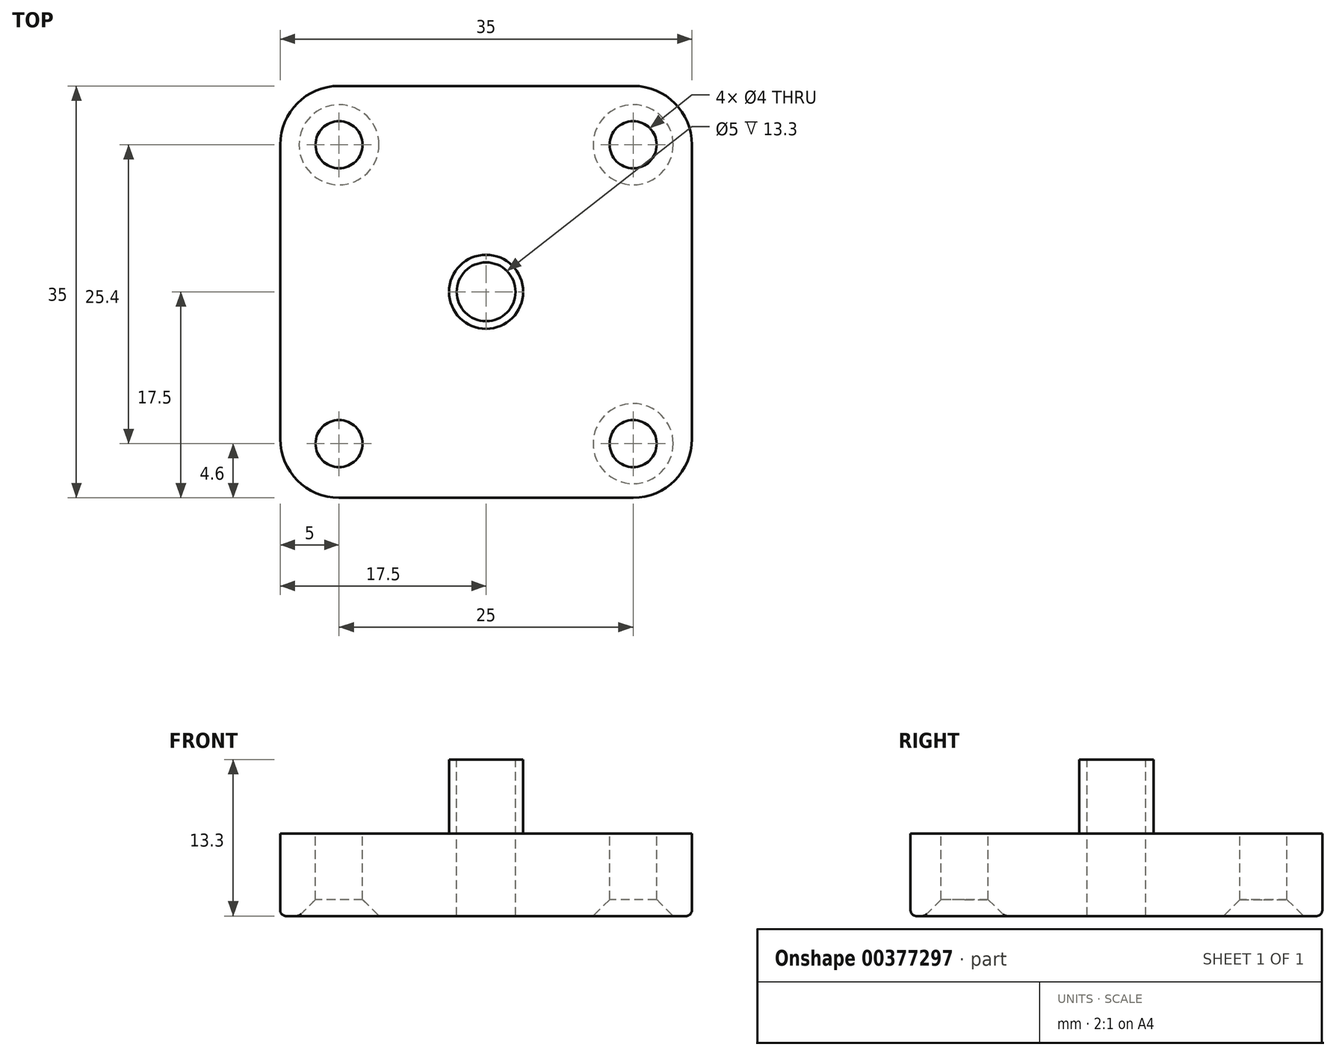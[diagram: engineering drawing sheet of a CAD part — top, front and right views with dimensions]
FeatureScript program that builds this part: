
annotation { "Feature Type Name" : "Feature", "Feature Type Description" : "" }
export const myFeature = defineFeature(function(context is Context, id is Id, definition is map)
    precondition{}
    {
        {
            var Q0;
            Q0=qCreatedBy(makeId("Top.planeOp"),FACE);
            var sketch = newSketch(context, id + "F0", { "sketchPlane" : qUnion([Q0])});
            skLineSegment(sketch, "E0.bottom", {"start": v(17.5, 17.5) * mm, "end": v(-17.5, 17.5) * mm});
            skLineSegment(sketch, "E0.top", {"start": v(17.5, -17.5) * mm, "end": v(-17.5, -17.5) * mm});
            skLineSegment(sketch, "E0.left", {"start": v(17.5, 17.5) * mm, "end": v(17.5, -17.5) * mm});
            skLineSegment(sketch, "E0.right", {"start": v(-17.5, 17.5) * mm, "end": v(-17.5, -17.5) * mm});
            skPoint(sketch, "E0.middle", {"position": v(0, 0) * mm});
            skSolve(sketch);
        }
        {
            var Q0;
            Q0=makeQuery(id+"F0.imprint","IMPRINT",FACE,{"disambiguationData":[TD([[makeQuery(id+"F0.imprint","IMPRINT",EDGE,{"derivedFrom":sQuery(id+"F0.wireOp",EDGE,"E0.bottom")}),1.0]])]});
            extrude(context, id + "F1", {"entities" : qUnion([Q0]), "endBound" : BoundingType.SYMMETRIC, "depth" : 7 * mm});
        }
        {
            var Q0;
            Q0=makeQuery(id+"F1.opExtrude","CAP_FACE",FACE,{"disambiguationData":[OSD([sQuery(id+"F0.wireOp",EDGE,"E0.bottom"),sQuery(id+"F0.wireOp",EDGE,"E0.top"),sQuery(id+"F0.wireOp",EDGE,"E0.left"),sQuery(id+"F0.wireOp",EDGE,"E0.right")])],"isStart":false});
            var sketch = newSketch(context, id + "F2", { "sketchPlane" : qUnion([Q0])});
            skCircle(sketch, "E1", {"center": v(-12.5, -12.9) * mm, "radius": 2 * mm});
            skCircle(sketch, "E2", {"center": v(-12.5, 12.5) * mm, "radius": 2 * mm});
            skCircle(sketch, "E3", {"center": v(12.5, 12.5) * mm, "radius": 2 * mm});
            skCircle(sketch, "E4", {"center": v(12.5, -12.9) * mm, "radius": 2 * mm});
            skSolve(sketch);
        }
        {
            var Q0;
            Q0 = qSketchRegion(id + "F2", true);
            extrude(context, id + "F3", {"entities" : qUnion([Q0]), "operationType" : NewBodyOperationType.REMOVE, "endBound" : BoundingType.THROUGH_ALL, "oppositeDirection" : true, "depth" : 25 * mm});
        }
        {
            var Q0;
            Q0=makeQuery(id+"F1.opExtrude","SWEPT_EDGE",EDGE,{"disambiguationData":[OSD([sQuery(id+"F0.wireOp",EDGE,"E0.bottom"),sQuery(id+"F0.wireOp",EDGE,"E0.right")])]});
            var Q1;
            Q1=makeQuery(id+"F1.opExtrude","SWEPT_EDGE",EDGE,{"disambiguationData":[OSD([sQuery(id+"F0.wireOp",EDGE,"E0.bottom"),sQuery(id+"F0.wireOp",EDGE,"E0.left")])]});
            var Q2;
            Q2=makeQuery(id+"F1.opExtrude","SWEPT_EDGE",EDGE,{"disambiguationData":[OSD([sQuery(id+"F0.wireOp",EDGE,"E0.top"),sQuery(id+"F0.wireOp",EDGE,"E0.left")])]});
            var Q3;
            Q3=makeQuery(id+"F1.opExtrude","SWEPT_EDGE",EDGE,{"disambiguationData":[OSD([sQuery(id+"F0.wireOp",EDGE,"E0.top"),sQuery(id+"F0.wireOp",EDGE,"E0.right")])]});
            fillet(context, id + "F4", {"entities" : qUnion([Q0, Q1, Q2, Q3]), "radius" : 5 * mm, "tangentPropagation" : true, "allowEdgeOverflow" : false});
        }
        {
            var Q0;
            Q0=makeQuery(id+"F1.opExtrude","CAP_FACE",FACE,{"disambiguationData":[OSD([sQuery(id+"F0.wireOp",EDGE,"E0.bottom"),sQuery(id+"F0.wireOp",EDGE,"E0.top"),sQuery(id+"F0.wireOp",EDGE,"E0.left"),sQuery(id+"F0.wireOp",EDGE,"E0.right")])],"isStart":false});
            var sketch = newSketch(context, id + "F5", { "sketchPlane" : qUnion([Q0])});
            skCircle(sketch, "E5", {"center": v(0, 0) * mm, "radius": 3.15 * mm});
            skSolve(sketch);
        }
        {
            var Q0;
            Q0 = qSketchRegion(id + "F5", true);
            extrude(context, id + "F6", {"entities" : qUnion([Q0]), "operationType" : NewBodyOperationType.ADD, "depth" : 6.3 * mm});
        }
        {
            var Q0;
            Q0=makeQuery(id+"F6.opExtrude","CAP_FACE",FACE,{"disambiguationData":[OSD([sQuery(id+"F5.wireOp",EDGE,"E5")])],"isStart":false});
            var sketch = newSketch(context, id + "F7", { "sketchPlane" : qUnion([Q0])});
            skCircle(sketch, "E6", {"center": v(0, 0) * mm, "radius": 2.5 * mm});
            skSolve(sketch);
        }
        {
            var Q0;
            Q0 = qSketchRegion(id + "F7", true);
            extrude(context, id + "F8", {"entities" : qUnion([Q0]), "operationType" : NewBodyOperationType.REMOVE, "endBound" : BoundingType.THROUGH_ALL, "oppositeDirection" : true, "depth" : 25 * mm});
        }
        {
            var Q0;
            Q0=makeQuery(id+"F3.boolean.opBoolean","INTERSECT",EDGE,{"derivedFrom":[makeQuery(id+"F1.opExtrude","CAP_FACE",FACE,{"disambiguationData":[OSD([sQuery(id+"F0.wireOp",EDGE,"E0.bottom"),sQuery(id+"F0.wireOp",EDGE,"E0.top"),sQuery(id+"F0.wireOp",EDGE,"E0.left"),sQuery(id+"F0.wireOp",EDGE,"E0.right")])],"isStart":true}),makeQuery(id+"F3.opExtrude","SWEPT_FACE",FACE,{"disambiguationData":[OSD([sQuery(id+"F2.wireOp",EDGE,"E1")])]})]});
            var Q1;
            Q1=makeQuery(id+"F3.boolean.opBoolean","INTERSECT",EDGE,{"derivedFrom":[makeQuery(id+"F1.opExtrude","CAP_FACE",FACE,{"disambiguationData":[OSD([sQuery(id+"F0.wireOp",EDGE,"E0.bottom"),sQuery(id+"F0.wireOp",EDGE,"E0.top"),sQuery(id+"F0.wireOp",EDGE,"E0.left"),sQuery(id+"F0.wireOp",EDGE,"E0.right")])],"isStart":true}),makeQuery(id+"F3.opExtrude","SWEPT_FACE",FACE,{"disambiguationData":[OSD([sQuery(id+"F2.wireOp",EDGE,"E4")])]})]});
            var Q2;
            Q2=makeQuery(id+"F3.boolean.opBoolean","INTERSECT",EDGE,{"derivedFrom":[makeQuery(id+"F1.opExtrude","CAP_FACE",FACE,{"disambiguationData":[OSD([sQuery(id+"F0.wireOp",EDGE,"E0.bottom"),sQuery(id+"F0.wireOp",EDGE,"E0.top"),sQuery(id+"F0.wireOp",EDGE,"E0.left"),sQuery(id+"F0.wireOp",EDGE,"E0.right")])],"isStart":true}),makeQuery(id+"F3.opExtrude","SWEPT_FACE",FACE,{"disambiguationData":[OSD([sQuery(id+"F2.wireOp",EDGE,"E3")])]})]});
            var Q3;
            Q3=makeQuery(id+"F3.boolean.opBoolean","INTERSECT",EDGE,{"derivedFrom":[makeQuery(id+"F1.opExtrude","CAP_FACE",FACE,{"disambiguationData":[OSD([sQuery(id+"F0.wireOp",EDGE,"E0.bottom"),sQuery(id+"F0.wireOp",EDGE,"E0.top"),sQuery(id+"F0.wireOp",EDGE,"E0.left"),sQuery(id+"F0.wireOp",EDGE,"E0.right")])],"isStart":true}),makeQuery(id+"F3.opExtrude","SWEPT_FACE",FACE,{"disambiguationData":[OSD([sQuery(id+"F2.wireOp",EDGE,"E2")])]})]});
            chamfer(context, id + "F9", {"entities" : qUnion([Q0, Q1, Q2, Q3]), "width" : 1.4 * mm, "tangentPropagation" : true});
        }
        {
            var Q0;
            {var subQ0=makeQuery(id+"F1.opExtrude","CAP_FACE",FACE,{"disambiguationData":[OSD([sQuery(id+"F0.wireOp",EDGE,"E0.bottom"),sQuery(id+"F0.wireOp",EDGE,"E0.top"),sQuery(id+"F0.wireOp",EDGE,"E0.left"),sQuery(id+"F0.wireOp",EDGE,"E0.right")])],"isStart":true});Q0=makeQuery(id+"F9.opChamfer","BLEND_EDGE",EDGE,{"blendedFrom":[makeQuery(id+"F3.boolean.opBoolean","INTERSECT",EDGE,{"derivedFrom":[subQ0,makeQuery(id+"F3.opExtrude","SWEPT_FACE",FACE,{"disambiguationData":[OSD([sQuery(id+"F2.wireOp",EDGE,"E1")])]})]}),subQ0],"blendedInto":[subQ0]});}
            var Q1;
            Q1=makeQuery(id+"F1.opExtrude","CAP_EDGE",EDGE,{"disambiguationData":[OSD([sQuery(id+"F0.wireOp",EDGE,"E0.right")])],"isStart":true});
            fillet(context, id + "F10", {"entities" : qUnion([Q0, Q1]), "radius" : .5 * mm, "tangentPropagation" : true, "allowEdgeOverflow" : false});
        }
    });
